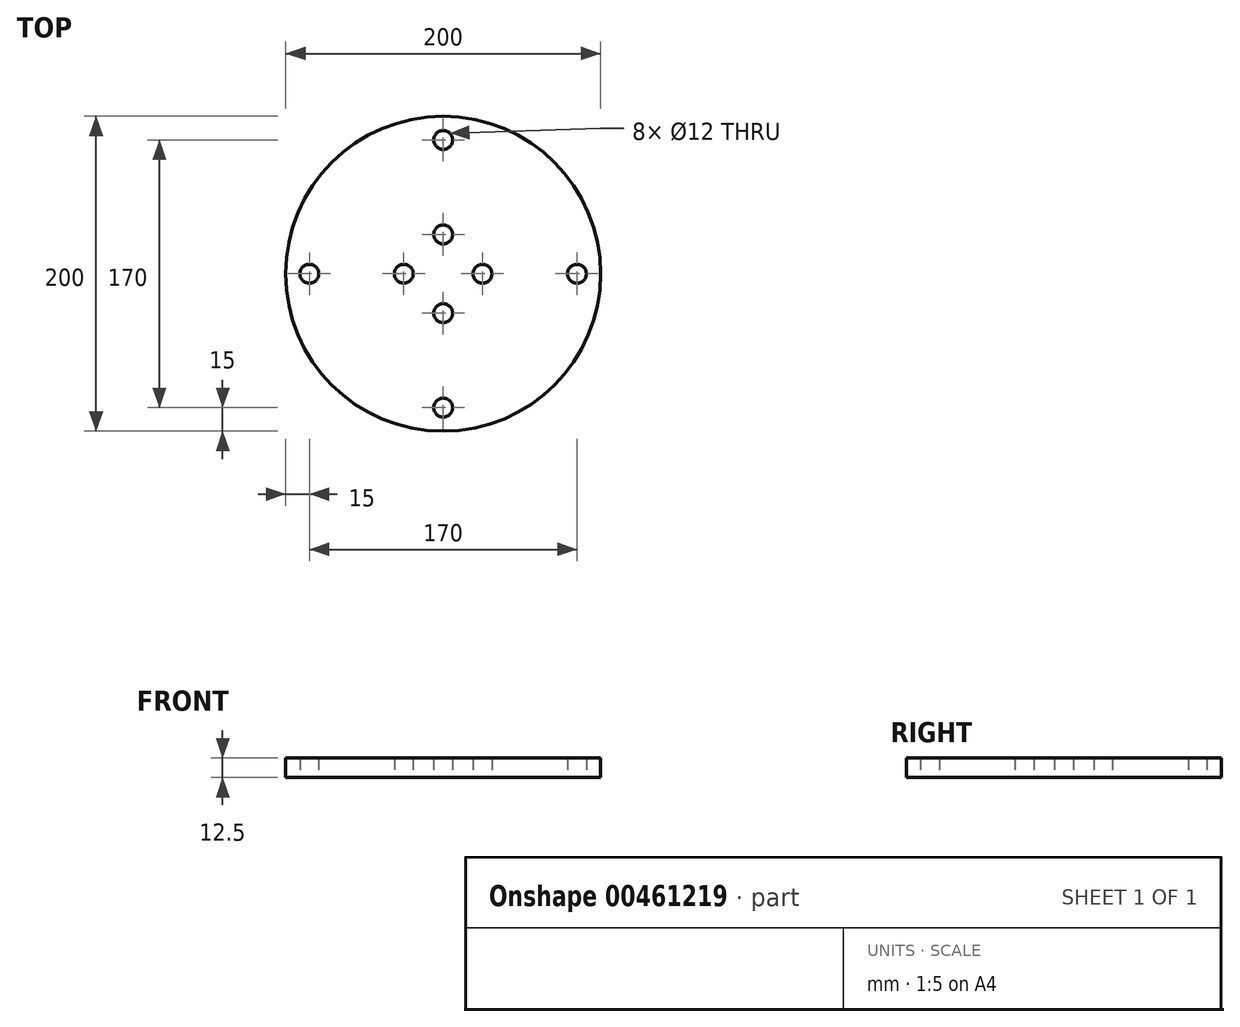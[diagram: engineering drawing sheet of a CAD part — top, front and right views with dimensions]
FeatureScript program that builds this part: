
annotation { "Feature Type Name" : "Feature", "Feature Type Description" : "" }
export const myFeature = defineFeature(function(context is Context, id is Id, definition is map)
    precondition{}
    {
        {
            var Q0;
            Q0=qCreatedBy(makeId("Top.planeOp"),FACE);
            var sketch = newSketch(context, id + "F0", { "sketchPlane" : qUnion([Q0])});
            skCircle(sketch, "E0", {"center": v(0, 0) * mm, "radius": 100 * mm});
            skCircle(sketch, "E1", {"center": v(0, 0) * mm, "radius": 85 * mm, "construction": true});
            skCircle(sketch, "E2", {"center": v(0, 85) * mm, "radius": 6 * mm});
            skCircle(sketch, "E3", {"center": v(85, 0) * mm, "radius": 6 * mm});
            skCircle(sketch, "E4", {"center": v(0, -85) * mm, "radius": 6 * mm});
            skCircle(sketch, "E5", {"center": v(-85, 0) * mm, "radius": 6 * mm});
            skLineSegment(sketch, "E6", {"start": v(0, 0) * mm, "end": v(25, 0) * mm, "construction": true});
            skLineSegment(sketch, "E7", {"start": v(25, 0) * mm, "end": v(-25, 0) * mm, "construction": true});
            skLineSegment(sketch, "E8", {"start": v(-25, 0) * mm, "end": v(0, 0) * mm, "construction": true});
            skLineSegment(sketch, "E9", {"start": v(0, 25) * mm, "end": v(0, -25) * mm, "construction": true});
            skLineSegment(sketch, "E10", {"start": v(0, 0) * mm, "end": v(0, 25) * mm, "construction": true});
            skCircle(sketch, "E11", {"center": v(0, 25) * mm, "radius": 6 * mm});
            skCircle(sketch, "E12", {"center": v(25, 0) * mm, "radius": 6 * mm});
            skCircle(sketch, "E13", {"center": v(0, -25) * mm, "radius": 6 * mm});
            skCircle(sketch, "E14", {"center": v(-25, 0) * mm, "radius": 6 * mm});
            skSolve(sketch);
        }
        {
            var Q0;
            Q0 = qSketchRegion(id + "F0", true);
            extrude(context, id + "F1", {"entities" : qUnion([Q0]), "depth" : 12.5 * mm});
        }
    });
